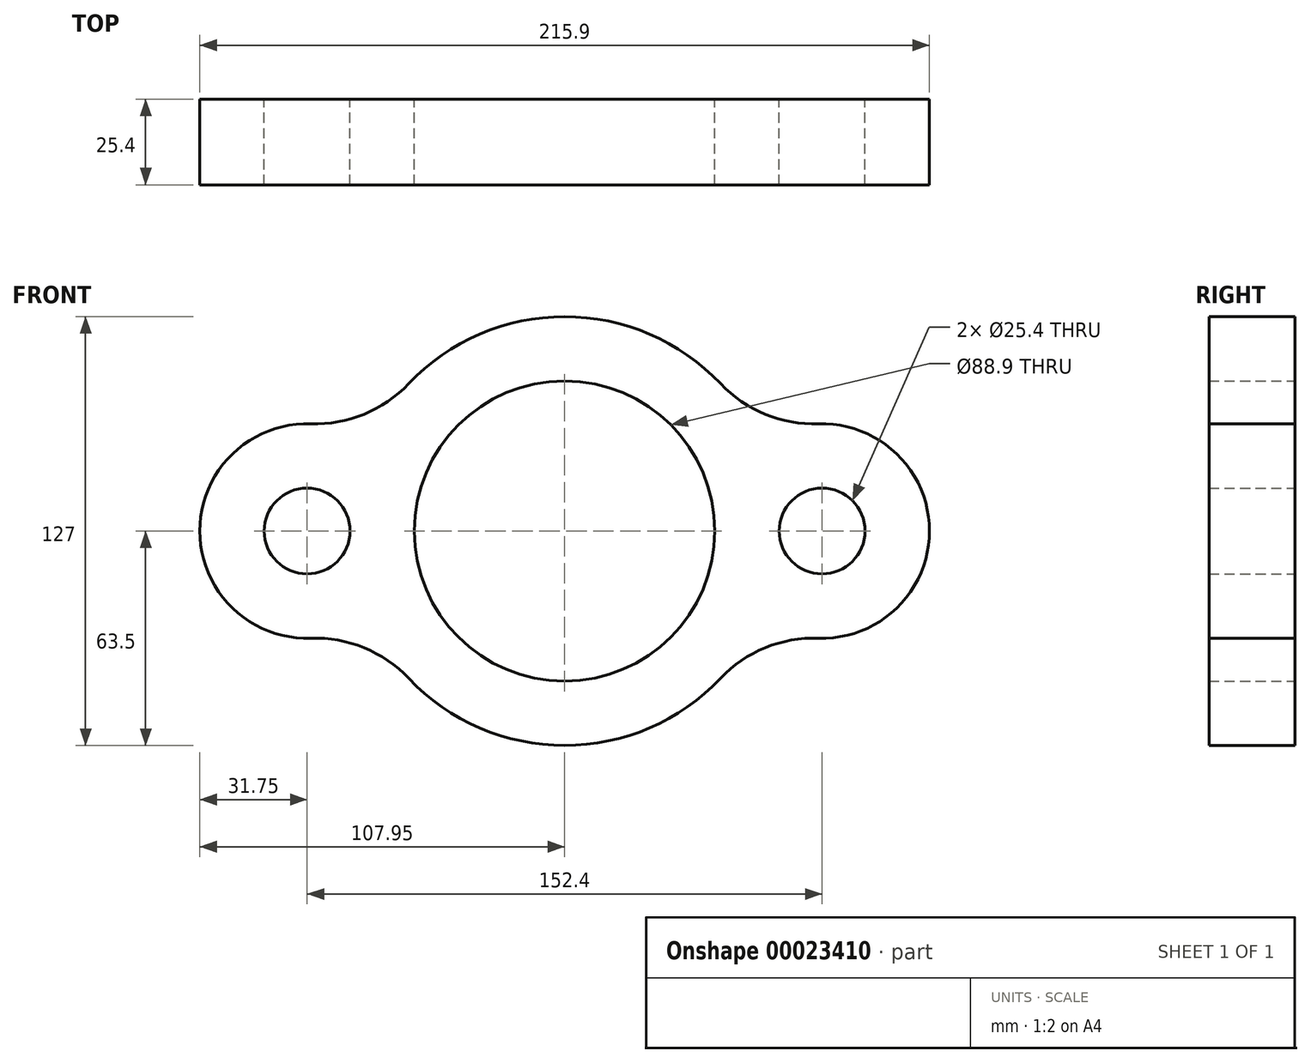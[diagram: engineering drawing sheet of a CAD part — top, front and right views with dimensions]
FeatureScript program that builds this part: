
annotation { "Feature Type Name" : "Feature", "Feature Type Description" : "" }
export const myFeature = defineFeature(function(context is Context, id is Id, definition is map)
    precondition{}
    {
        {
            var Q0;
            Q0=qCreatedBy(makeId("Front.planeOp"),FACE);
            var sketch = newSketch(context, id + "F0", { "sketchPlane" : qUnion([Q0])});
            skCircle(sketch, "E0", {"center": v(0, 0) * mm, "radius": 63.5 * mm});
            skCircle(sketch, "E1", {"center": v(-76.2, 0) * mm, "radius": 31.75 * mm});
            skCircle(sketch, "E2", {"center": v(76.2, 0) * mm, "radius": 31.75 * mm});
            skCircle(sketch, "E3", {"center": v(76.2, 0) * mm, "radius": 12.7 * mm});
            skCircle(sketch, "E4", {"center": v(-76.2, 0) * mm, "radius": 12.7 * mm});
            skCircle(sketch, "E5", {"center": v(0, 0) * mm, "radius": 44.45 * mm});
            skArc(sketch, "E6", {"start": v(-75.12, 31.73) * mm, "mid": v(-59.35, 34.56) * mm, "end": v(-46.14, 43.63) * mm});
            skArc(sketch, "E7", {"start": v(-46.14, -43.63) * mm, "mid": v(-59.35, -34.56) * mm, "end": v(-75.12, -31.73) * mm});
            skArc(sketch, "E8", {"start": v(46.14, 43.63) * mm, "mid": v(59.35, 34.56) * mm, "end": v(75.12, 31.73) * mm});
            skArc(sketch, "E9", {"start": v(75.12, -31.73) * mm, "mid": v(59.35, -34.56) * mm, "end": v(46.14, -43.63) * mm});
            skSolve(sketch);
        }
        {
            var Q0;
            {var subQ0=sQuery(id+"F0.wireOp",EDGE,"E6");Q0=makeQuery(id+"F0.imprint","IMPRINT",FACE,{"disambiguationData":[TD([[makeQuery(id+"F0.imprint","IMPRINT",EDGE,{"derivedFrom":subQ0}),-1.0]])]});}
            var Q1;
            {var subQ0=sQuery(id+"F0.wireOp",EDGE,"E8");Q1=makeQuery(id+"F0.imprint","IMPRINT",FACE,{"disambiguationData":[TD([[makeQuery(id+"F0.imprint","IMPRINT",EDGE,{"derivedFrom":subQ0}),-1.0]])]});}
            var Q2;
            {var subQ0=sQuery(id+"F0.wireOp",EDGE,"E7");Q2=makeQuery(id+"F0.imprint","IMPRINT",FACE,{"disambiguationData":[TD([[makeQuery(id+"F0.imprint","IMPRINT",EDGE,{"derivedFrom":subQ0}),-1.0]])]});}
            var Q3;
            {var subQ2=sQuery(id+"F0.wireOp",EDGE,"E0");var subQ5=makeQuery(id+"F0.imprint","INTERSECT",VERTEX,{"derivedFrom":[subQ2,sQuery(id+"F0.wireOp",EDGE,"E3")]});Q3=makeQuery(id+"F0.imprint","IMPRINT",FACE,{"disambiguationData":[TD([[makeQuery(id+"F0.imprint","IMPRINT",EDGE,{"disambiguationData":[TD([[subQ5,-1.0]])],"derivedFrom":subQ2}),1.0]])]});}
            var Q4;
            {var subQ0=sQuery(id+"F0.wireOp",EDGE,"E9");Q4=makeQuery(id+"F0.imprint","IMPRINT",FACE,{"disambiguationData":[TD([[makeQuery(id+"F0.imprint","IMPRINT",EDGE,{"derivedFrom":subQ0}),-1.0]])]});}
            var Q5;
            {var subQ2=sQuery(id+"F0.wireOp",EDGE,"E0");var subQ5=makeQuery(id+"F0.imprint","INTERSECT",VERTEX,{"derivedFrom":[subQ2,sQuery(id+"F0.wireOp",EDGE,"E4")]});Q5=makeQuery(id+"F0.imprint","IMPRINT",FACE,{"disambiguationData":[TD([[makeQuery(id+"F0.imprint","IMPRINT",EDGE,{"disambiguationData":[TD([[subQ5,1.0]])],"derivedFrom":subQ2}),1.0]])]});}
            var Q6;
            {var subQ5=sQuery(id+"F0.wireOp",EDGE,"E0");var subQ9=makeQuery(id+"F0.imprint","INTERSECT",VERTEX,{"derivedFrom":[subQ5,sQuery(id+"F0.wireOp",EDGE,"E8")]});Q6=makeQuery(id+"F0.imprint","IMPRINT",FACE,{"disambiguationData":[TD([[makeQuery(id+"F0.imprint","IMPRINT",EDGE,{"disambiguationData":[TD([[subQ9,1.0]])],"derivedFrom":subQ5}),1.0]])]});}
            var Q7;
            {var subQ0=sQuery(id+"F0.wireOp",EDGE,"E3");Q7=makeQuery(id+"F0.imprint","IMPRINT",FACE,{"disambiguationData":[TD([[makeQuery(id+"F0.imprint","IMPRINT",EDGE,{"derivedFrom":subQ0}),-1.0]])]});}
            var Q8;
            {var subQ0=sQuery(id+"F0.wireOp",EDGE,"E4");Q8=makeQuery(id+"F0.imprint","IMPRINT",FACE,{"disambiguationData":[TD([[makeQuery(id+"F0.imprint","IMPRINT",EDGE,{"derivedFrom":subQ0}),-1.0]])]});}
            var Q9;
            {var subQ5=sQuery(id+"F0.wireOp",EDGE,"E0");var subQ9=makeQuery(id+"F0.imprint","INTERSECT",VERTEX,{"derivedFrom":[subQ5,sQuery(id+"F0.wireOp",EDGE,"E7")]});Q9=makeQuery(id+"F0.imprint","IMPRINT",FACE,{"disambiguationData":[TD([[makeQuery(id+"F0.imprint","IMPRINT",EDGE,{"disambiguationData":[TD([[subQ9,1.0]])],"derivedFrom":subQ5}),1.0]])]});}
            extrude(context, id + "F1", {"entities" : qUnion([Q0, Q1, Q2, Q3, Q4, Q5, Q6, Q7, Q8, Q9]), "depth" : 25.4 * mm});
        }
    });
